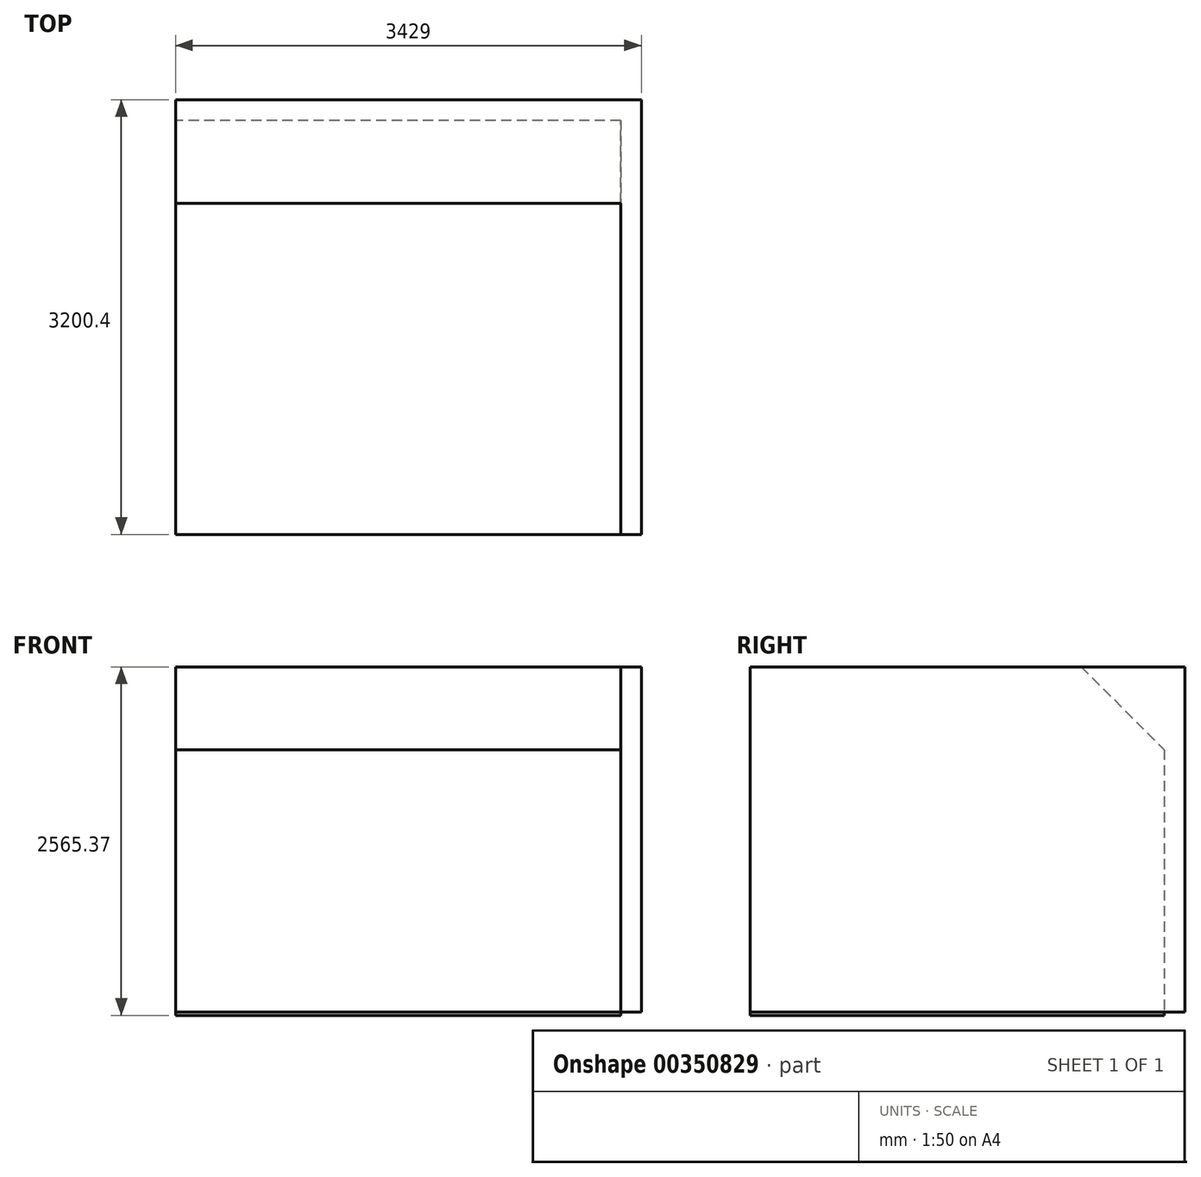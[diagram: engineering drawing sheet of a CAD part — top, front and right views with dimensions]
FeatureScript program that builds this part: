
annotation { "Feature Type Name" : "Feature", "Feature Type Description" : "" }
export const myFeature = defineFeature(function(context is Context, id is Id, definition is map)
    precondition{}
    {
        {
            var Q0;
            Q0=qCreatedBy(makeId("Top.planeOp"),FACE);
            var sketch = newSketch(context, id + "F0", { "sketchPlane" : qUnion([Q0])});
            skLineSegment(sketch, "E0.bottom", {"start": v(-488.9, -318.15) * mm, "end": v(2787.7, -318.15) * mm});
            skLineSegment(sketch, "E0.top", {"start": v(-488.9, -3366.15) * mm, "end": v(2787.7, -3366.15) * mm});
            skLineSegment(sketch, "E0.left", {"start": v(-488.9, -318.15) * mm, "end": v(-488.9, -3366.15) * mm});
            skLineSegment(sketch, "E0.right", {"start": v(2787.7, -318.15) * mm, "end": v(2787.7, -3366.15) * mm});
            skSolve(sketch);
        }
        {
            var Q0;
            Q0 = qSketchRegion(id + "F0", true);
            extrude(context, id + "F1", {"entities" : qUnion([Q0]), "depth" : 25.4 * mm});
        }
        {
            var Q0;
            Q0=makeQuery(id+"F1.opExtrude","CAP_FACE",FACE,{"disambiguationData":[OSD([sQuery(id+"F0.wireOp",EDGE,"E0.bottom"),sQuery(id+"F0.wireOp",EDGE,"E0.top"),sQuery(id+"F0.wireOp",EDGE,"E0.left"),sQuery(id+"F0.wireOp",EDGE,"E0.right")])],"isStart":false});
            var sketch = newSketch(context, id + "F2", { "sketchPlane" : qUnion([Q0])});
            skLineSegment(sketch, "E1.bottom", {"start": v(-488.9, -318.15) * mm, "end": v(2787.7, -318.15) * mm});
            skLineSegment(sketch, "E1.top", {"start": v(-488.9, -165.75) * mm, "end": v(2940.1, -165.75) * mm});
            skLineSegment(sketch, "E1.left", {"start": v(-488.9, -165.75) * mm, "end": v(-488.9, -318.15) * mm});
            skLineSegment(sketch, "E2.top", {"start": v(2940.1, -3366.15) * mm, "end": v(2787.7, -3366.15) * mm});
            skLineSegment(sketch, "E2.left", {"start": v(2787.7, -318.15) * mm, "end": v(2787.7, -3366.15) * mm});
            skLineSegment(sketch, "E2.right", {"start": v(2940.1, -165.75) * mm, "end": v(2940.1, -3366.15) * mm});
            skSolve(sketch);
        }
        {
            var Q0;
            Q0 = qSketchRegion(id + "F2", true);
            extrude(context, id + "F3", {"entities" : qUnion([Q0]), "operationType" : NewBodyOperationType.ADD, "depth" : 2539.97 * mm});
        }
        {
            var Q0;
            Q0=makeQuery(id+"F3.opExtrude","SWEPT_FACE",FACE,{"disambiguationData":[OSD([sQuery(id+"F2.wireOp",EDGE,"E1.left")])]});
            var sketch = newSketch(context, id + "F4", { "sketchPlane" : qUnion([Q0])});
            skLineSegment(sketch, "E3", {"start": v(318.15, 2565.37) * mm, "end": v(927.72, 2565.37) * mm});
            skLineSegment(sketch, "E4", {"start": v(927.72, 2565.37) * mm, "end": v(318.15, 1955.8) * mm});
            skLineSegment(sketch, "E5", {"start": v(318.15, 1955.8) * mm, "end": v(318.15, 2565.37) * mm});
            skSolve(sketch);
        }
        {
            var Q0;
            Q0 = qSketchRegion(id + "F4", true);
            var Q1;
            Q1=makeQuery(id+"F3.opExtrude","SWEPT_FACE",FACE,{"disambiguationData":[OSD([sQuery(id+"F2.wireOp",EDGE,"E2.left")])]});
            extrude(context, id + "F5", {"entities" : qUnion([Q0]), "operationType" : NewBodyOperationType.ADD, "endBound" : BoundingType.UP_TO_SURFACE, "oppositeDirection" : true, "endBoundEntityFace" : qUnion([Q1]), "depth" : 939.8 * mm});
        }
    });
